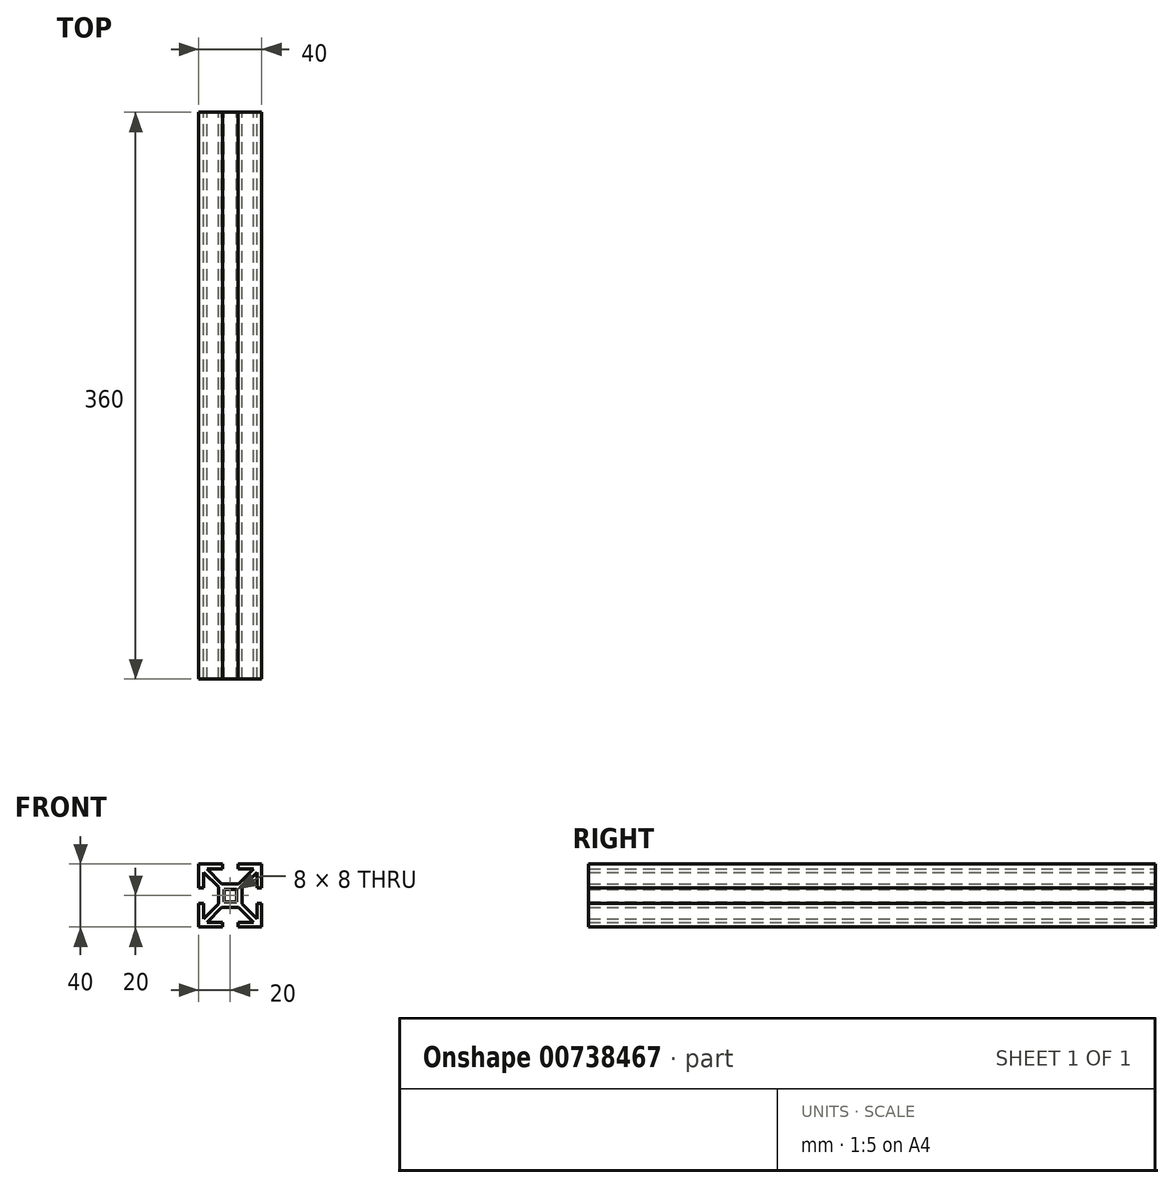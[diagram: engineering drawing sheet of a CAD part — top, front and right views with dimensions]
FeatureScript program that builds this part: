
annotation { "Feature Type Name" : "Feature", "Feature Type Description" : "" }
export const myFeature = defineFeature(function(context is Context, id is Id, definition is map)
    precondition{}
    {
        {
            var Q0;
            Q0=qCreatedBy(makeId("Front.planeOp"),FACE);
            var sketch = newSketch(context, id + "F0", { "sketchPlane" : qUnion([Q0])});
            skPoint(sketch, "E0.middle", {"position": v(0, 0) * mm});
            skLineSegment(sketch, "E1.bottom", {"start": v(20, 20) * mm, "end": v(-20, 20) * mm});
            skLineSegment(sketch, "E1.top", {"start": v(20, -20) * mm, "end": v(-20, -20) * mm});
            skLineSegment(sketch, "E1.left", {"start": v(20, 20) * mm, "end": v(20, -20) * mm});
            skLineSegment(sketch, "E1.right", {"start": v(-20, 20) * mm, "end": v(-20, -20) * mm});
            skLineSegment(sketch, "E2.bottom", {"start": v(4, 4) * mm, "end": v(-4, 4) * mm});
            skLineSegment(sketch, "E2.top", {"start": v(4, -4) * mm, "end": v(-4, -4) * mm});
            skLineSegment(sketch, "E2.left", {"start": v(4, 4) * mm, "end": v(4, -4) * mm});
            skLineSegment(sketch, "E2.right", {"start": v(-4, 4) * mm, "end": v(-4, -4) * mm});
            skLineSegment(sketch, "E3.bottom", {"start": v(7.5, -7.5) * mm, "end": v(-7.5, -7.5) * mm});
            skLineSegment(sketch, "E3.top", {"start": v(7.5, 7.5) * mm, "end": v(-7.5, 7.5) * mm});
            skLineSegment(sketch, "E3.left", {"start": v(7.5, -7.5) * mm, "end": v(7.5, 7.5) * mm});
            skLineSegment(sketch, "E3.right", {"start": v(-7.5, -7.5) * mm, "end": v(-7.5, 7.5) * mm});
            skLineSegment(sketch, "E4", {"start": v(-5, 20) * mm, "end": v(-5, -20) * mm, "construction": true});
            skLineSegment(sketch, "E5", {"start": v(5, -20) * mm, "end": v(5, 20) * mm, "construction": true});
            skLineSegment(sketch, "E6", {"start": v(-20, 5) * mm, "end": v(20, 5) * mm, "construction": true});
            skLineSegment(sketch, "E7", {"start": v(-20, -5) * mm, "end": v(20, -5) * mm, "construction": true});
            skLineSegment(sketch, "E8.bottom", {"start": v(17, 17) * mm, "end": v(-17, 17) * mm});
            skLineSegment(sketch, "E8.top", {"start": v(17, -17) * mm, "end": v(-17, -17) * mm});
            skLineSegment(sketch, "E8.left", {"start": v(17, 17) * mm, "end": v(17, -17) * mm});
            skLineSegment(sketch, "E8.right", {"start": v(-17, 17) * mm, "end": v(-17, -17) * mm});
            skLineSegment(sketch, "E9", {"start": v(0, 0) * mm, "end": v(20, 20) * mm, "construction": true});
            skLineSegment(sketch, "E10", {"start": v(0, 0) * mm, "end": v(20, -20) * mm, "construction": true});
            skLineSegment(sketch, "E11", {"start": v(0, 0) * mm, "end": v(-20, -20) * mm, "construction": true});
            skLineSegment(sketch, "E12", {"start": v(0, 0) * mm, "end": v(-20, 20) * mm, "construction": true});
            skLineSegment(sketch, "E13", {"start": v(5.38, 7.5) * mm, "end": v(14.88, 17) * mm});
            skLineSegment(sketch, "E14", {"start": v(7.5, 5.38) * mm, "end": v(17, 14.88) * mm});
            skLineSegment(sketch, "E15", {"start": v(7.5, -5.38) * mm, "end": v(17, -14.88) * mm});
            skLineSegment(sketch, "E16", {"start": v(5.38, -7.5) * mm, "end": v(14.88, -17) * mm});
            skLineSegment(sketch, "E17", {"start": v(-7.5, -5.38) * mm, "end": v(-17, -14.88) * mm});
            skLineSegment(sketch, "E18", {"start": v(-14.88, -17) * mm, "end": v(-5.38, -7.5) * mm});
            skLineSegment(sketch, "E19", {"start": v(-5.38, 7.5) * mm, "end": v(-14.88, 17) * mm});
            skLineSegment(sketch, "E20", {"start": v(-7.5, 5.38) * mm, "end": v(-17, 14.88) * mm});
            skLineSegment(sketch, "E21", {"start": v(-5, 20) * mm, "end": v(-5, 17) * mm});
            skLineSegment(sketch, "E22", {"start": v(5, 20) * mm, "end": v(5, 17) * mm});
            skLineSegment(sketch, "E23", {"start": v(17, 5) * mm, "end": v(20, 5) * mm});
            skLineSegment(sketch, "E24", {"start": v(17, -5) * mm, "end": v(20, -5) * mm});
            skLineSegment(sketch, "E25", {"start": v(5, -17) * mm, "end": v(5, -20) * mm});
            skLineSegment(sketch, "E26", {"start": v(-5, -17) * mm, "end": v(-5, -20) * mm});
            skLineSegment(sketch, "E27", {"start": v(-17, -5) * mm, "end": v(-20, -5) * mm});
            skLineSegment(sketch, "E28", {"start": v(-17, 5) * mm, "end": v(-20, 5) * mm});
            skSolve(sketch);
        }
        {
            var Q0;
            {var subQ2=sQuery(id+"F0.wireOp",EDGE,"E21");Q0=makeQuery(id+"F0.imprint","IMPRINT",FACE,{"disambiguationData":[TD([[makeQuery(id+"F0.imprint","IMPRINT",EDGE,{"derivedFrom":subQ2}),-1.0]])]});}
            var Q1;
            {var subQ4=sQuery(id+"F0.wireOp",EDGE,"E26");Q1=makeQuery(id+"F0.imprint","IMPRINT",FACE,{"disambiguationData":[TD([[makeQuery(id+"F0.imprint","IMPRINT",EDGE,{"derivedFrom":subQ4}),-1.0]])]});}
            var Q2;
            {var subQ8=sQuery(id+"F0.wireOp",EDGE,"E24");Q2=makeQuery(id+"F0.imprint","IMPRINT",FACE,{"disambiguationData":[TD([[makeQuery(id+"F0.imprint","IMPRINT",EDGE,{"derivedFrom":subQ8}),-1.0]])]});}
            var Q3;
            {var subQ2=sQuery(id+"F0.wireOp",EDGE,"E22");Q3=makeQuery(id+"F0.imprint","IMPRINT",FACE,{"disambiguationData":[TD([[makeQuery(id+"F0.imprint","IMPRINT",EDGE,{"derivedFrom":subQ2}),1.0]])]});}
            var Q4;
            {var subQ4=sQuery(id+"F0.wireOp",EDGE,"E13");Q4=makeQuery(id+"F0.imprint","IMPRINT",FACE,{"disambiguationData":[TD([[makeQuery(id+"F0.imprint","IMPRINT",EDGE,{"derivedFrom":subQ4}),-1.0]])]});}
            var Q5;
            {var subQ4=sQuery(id+"F0.wireOp",EDGE,"E19");Q5=makeQuery(id+"F0.imprint","IMPRINT",FACE,{"disambiguationData":[TD([[makeQuery(id+"F0.imprint","IMPRINT",EDGE,{"derivedFrom":subQ4}),1.0]])]});}
            var Q6;
            {var subQ3=sQuery(id+"F0.wireOp",EDGE,"E17");Q6=makeQuery(id+"F0.imprint","IMPRINT",FACE,{"disambiguationData":[TD([[makeQuery(id+"F0.imprint","IMPRINT",EDGE,{"derivedFrom":subQ3}),1.0]])]});}
            var Q7;
            {var subQ7=sQuery(id+"F0.wireOp",EDGE,"E15");Q7=makeQuery(id+"F0.imprint","IMPRINT",FACE,{"disambiguationData":[TD([[makeQuery(id+"F0.imprint","IMPRINT",EDGE,{"derivedFrom":subQ7}),-1.0]])]});}
            var Q8;
            Q8=makeQuery(id+"F0.imprint","IMPRINT",FACE,{"disambiguationData":[TD([[makeQuery(id+"F0.imprint","IMPRINT",EDGE,{"derivedFrom":sQuery(id+"F0.wireOp",EDGE,"E2.bottom")}),-1.0]])]});
            extrude(context, id + "F1", {"entities" : qUnion([Q0, Q1, Q2, Q3, Q4, Q5, Q6, Q7, Q8]), "endBound" : BoundingType.SYMMETRIC, "depth" : 360 * mm, "offsetDistance" : 25 * mm});
        }
    });
